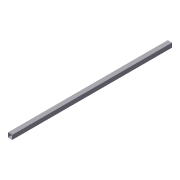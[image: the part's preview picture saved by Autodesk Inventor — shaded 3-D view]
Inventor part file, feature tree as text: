
AUTODESK INVENTOR PART (.ipt)
format: ipt  version: 2012 (Build 160160000, 160)  size: 71,168 bytes
history: native  units: in
note: dims shown in document units (in); Inventor stores cm internally (conversion verified against a paired STEP export)
features: extrude x1, shell x1, sketch x1
ambient origin geometry x8: Origin, YZ Plane, XZ Plane, XY Plane, X Axis, Y Axis, Z Axis, Center Point
bodies: Solid1 (feature_tree)
feature tree (3):
  extrude  "Extrusion1"  Depth=1.0in
  shell  "Shell1"  Thickness=37.0in
  sketch  "Sketch1"  dims[d0=1.0in d1=1.0in d2=37.0in d3=0.0in d4=0.0625in]
